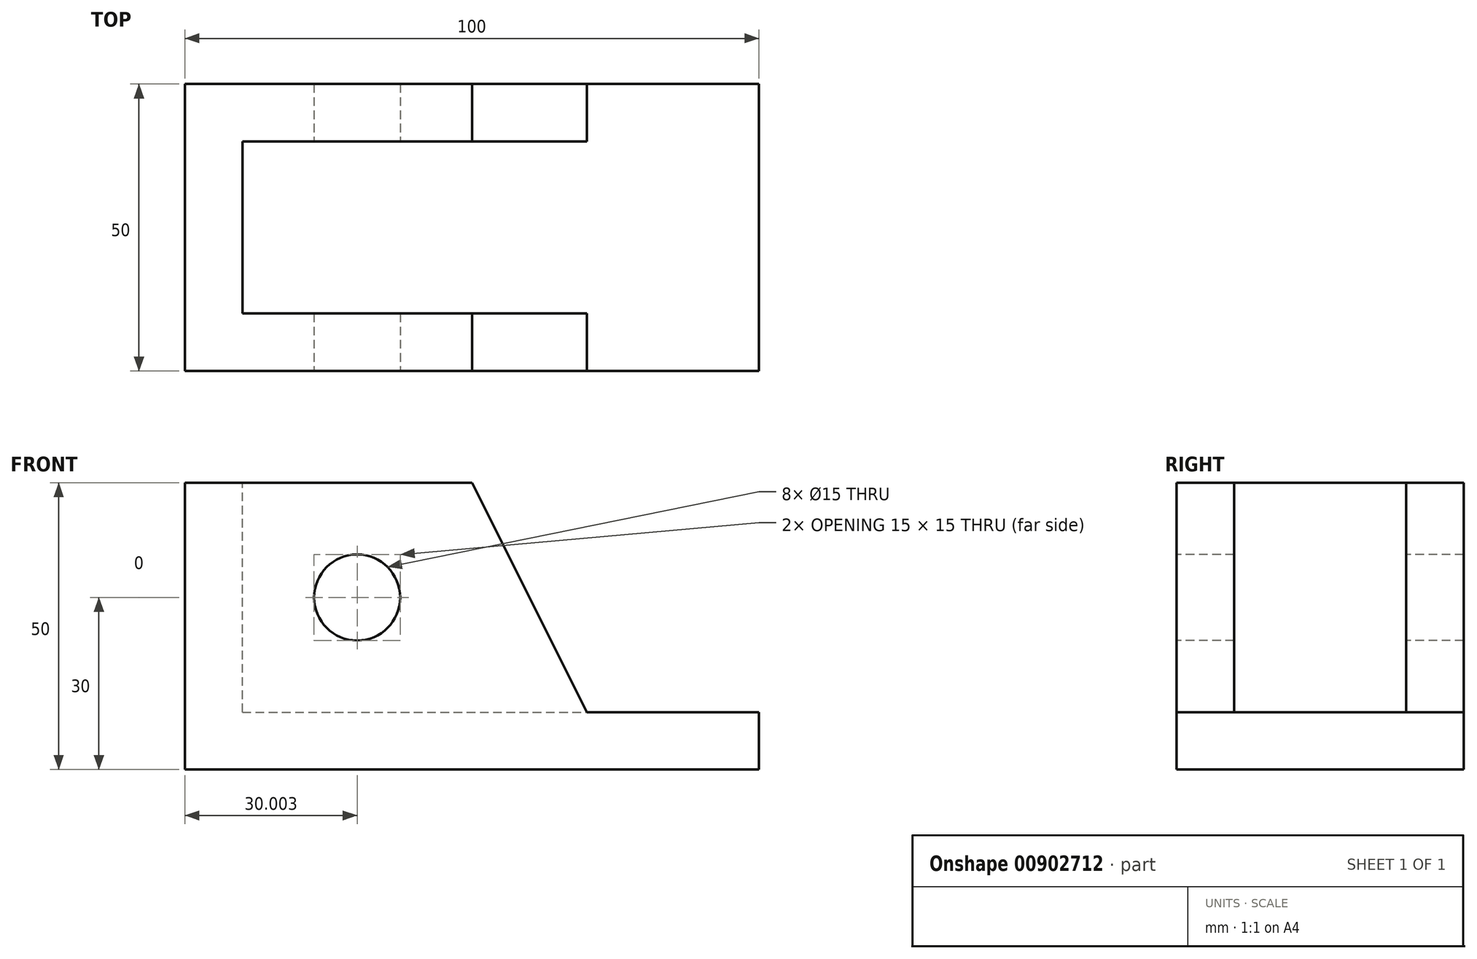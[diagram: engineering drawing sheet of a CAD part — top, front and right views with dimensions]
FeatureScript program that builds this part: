
annotation { "Feature Type Name" : "Feature", "Feature Type Description" : "" }
export const myFeature = defineFeature(function(context is Context, id is Id, definition is map)
    precondition{}
    {
        {
            var Q0;
            Q0=qCreatedBy(makeId("Top.planeOp"),FACE);
            var sketch = newSketch(context, id + "F0", { "sketchPlane" : qUnion([Q0])});
            skLineSegment(sketch, "E0", {"start": v(-73.6, 0) * mm, "end": v(77.2, 0) * mm, "construction": true});
            skLineSegment(sketch, "E1.0", {"start": v(-33.94, 25) * mm, "end": v(66.06, 25) * mm});
            skLineSegment(sketch, "E2", {"start": v(-33.94, 25) * mm, "end": v(-33.94, -25) * mm});
            skLineSegment(sketch, "E3.MirrorCS", {"start": v(-33.94, -25) * mm, "end": v(66.06, -25) * mm});
            skLineSegment(sketch, "E4.filletArc", {"start": v(-33.94, 25) * mm, "end": v(-33.94, 25) * mm});
            skLineSegment(sketch, "E5.filletArc", {"start": v(-33.94, -25) * mm, "end": v(-33.94, -25) * mm});
            skLineSegment(sketch, "E6.0", {"start": v(66.06, 25) * mm, "end": v(66.06, -25) * mm});
            skLineSegment(sketch, "E7.filletArc", {"start": v(66.06, 25) * mm, "end": v(66.06, 25) * mm});
            skLineSegment(sketch, "E8.filletArc", {"start": v(66.06, -25) * mm, "end": v(66.06, -25) * mm});
            skSolve(sketch);
        }
        {
            var Q0;
            Q0=makeQuery(id+"F0.imprint","IMPRINT",FACE,{"disambiguationData":[TD([[makeQuery(id+"F0.imprint","IMPRINT",EDGE,{"derivedFrom":sQuery(id+"F0.wireOp",EDGE,"E1.0")}),-1.0]])]});
            extrude(context, id + "F1", {"entities" : qUnion([Q0]), "depth" : 50 * mm, "offsetDistance" : 25 * mm});
        }
        {
            var Q0;
            Q0=makeQuery(id+"F1.opExtrude","SWEPT_FACE",FACE,{"disambiguationData":[OSD([sQuery(id+"F0.wireOp",EDGE,"E3.MirrorCS")])]});
            var sketch = newSketch(context, id + "F2", { "sketchPlane" : qUnion([Q0])});
            skLineSegment(sketch, "E9", {"start": v(16.06, 50) * mm, "end": v(36.06, 10) * mm});
            skLineSegment(sketch, "E10", {"start": v(36.06, 10) * mm, "end": v(66.06, 10) * mm});
            skLineSegment(sketch, "E11", {"start": v(66.06, 10) * mm, "end": v(66.06, 50) * mm});
            skLineSegment(sketch, "E12", {"start": v(66.06, 50) * mm, "end": v(16.06, 50) * mm});
            skSolve(sketch);
        }
        {
            var Q0;
            Q0=makeQuery(id+"F2.imprint","IMPRINT",FACE,{"disambiguationData":[TD([[makeQuery(id+"F2.imprint","IMPRINT",EDGE,{"derivedFrom":sQuery(id+"F2.wireOp",EDGE,"E9")}),1.0]])]});
            extrude(context, id + "F3", {"entities" : qUnion([Q0]), "operationType" : NewBodyOperationType.REMOVE, "endBound" : BoundingType.THROUGH_ALL, "oppositeDirection" : true, "depth" : 25 * mm, "offsetDistance" : 25 * mm});
        }
        {
            var Q0;
            Q0=makeQuery(id+"F1.opExtrude","CAP_FACE",FACE,{"disambiguationData":[OSD([sQuery(id+"F0.wireOp",EDGE,"E1.0"),sQuery(id+"F0.wireOp",EDGE,"E2"),sQuery(id+"F0.wireOp",EDGE,"E3.MirrorCS"),sQuery(id+"F0.wireOp",EDGE,"E6.0")])],"isStart":false});
            var sketch = newSketch(context, id + "F4", { "sketchPlane" : qUnion([Q0])});
            skLineSegment(sketch, "E13.0", {"start": v(-23.94, 15) * mm, "end": v(66.06, 15) * mm});
            skLineSegment(sketch, "E14.MirrorCS", {"start": v(-23.94, -15) * mm, "end": v(66.06, -15) * mm});
            skLineSegment(sketch, "E15.0", {"start": v(-23.94, 15) * mm, "end": v(-23.94, -15) * mm});
            skLineSegment(sketch, "E16.filletArc", {"start": v(-23.94, -15) * mm, "end": v(-23.94, -15) * mm});
            skLineSegment(sketch, "E17.filletArc", {"start": v(-23.94, 15) * mm, "end": v(-23.94, 15) * mm});
            skLineSegment(sketch, "E18.0", {"start": v(66.06, 15) * mm, "end": v(66.06, -15) * mm});
            skLineSegment(sketch, "E19.filletArc", {"start": v(66.06, 15) * mm, "end": v(66.06, 15) * mm});
            skLineSegment(sketch, "E20.filletArc", {"start": v(66.06, -15) * mm, "end": v(66.06, -15) * mm});
            skSolve(sketch);
        }
        {
            var Q0;
            {var subQ0=sQuery(id+"F4.wireOp",EDGE,"E18.0");Q0=makeQuery(id+"F4.imprint","IMPRINT",FACE,{"disambiguationData":[TD([[makeQuery(id+"F4.imprint","IMPRINT",EDGE,{"derivedFrom":subQ0}),-1.0]])]});}
            var Q1;
            {var subQ0=sQuery(id+"F4.wireOp",EDGE,"E15.0");Q1=makeQuery(id+"F4.imprint","IMPRINT",FACE,{"disambiguationData":[TD([[makeQuery(id+"F4.imprint","IMPRINT",EDGE,{"derivedFrom":subQ0}),1.0]])]});}
            extrude(context, id + "F5", {"entities" : qUnion([Q0, Q1]), "operationType" : NewBodyOperationType.REMOVE, "oppositeDirection" : true, "depth" : 40 * mm, "offsetDistance" : 25 * mm});
        }
        {
            var Q0;
            Q0=makeQuery(id+"F1.opExtrude","SWEPT_FACE",FACE,{"disambiguationData":[OSD([sQuery(id+"F0.wireOp",EDGE,"E3.MirrorCS")])]});
            var sketch = newSketch(context, id + "F6", { "sketchPlane" : qUnion([Q0])});
            skCircle(sketch, "E21", {"center": v(-3.94, 30) * mm, "radius": 7.5 * mm});
            skSolve(sketch);
        }
        {
            var Q0;
            Q0=makeQuery(id+"F6.imprint","IMPRINT",FACE,{"disambiguationData":[TD([[makeQuery(id+"F6.imprint","IMPRINT",EDGE,{"derivedFrom":sQuery(id+"F6.wireOp",EDGE,"E21")}),1.0]])]});
            extrude(context, id + "F7", {"entities" : qUnion([Q0]), "operationType" : NewBodyOperationType.REMOVE, "endBound" : BoundingType.THROUGH_ALL, "oppositeDirection" : true, "depth" : 25 * mm, "offsetDistance" : 25 * mm});
        }
    });
